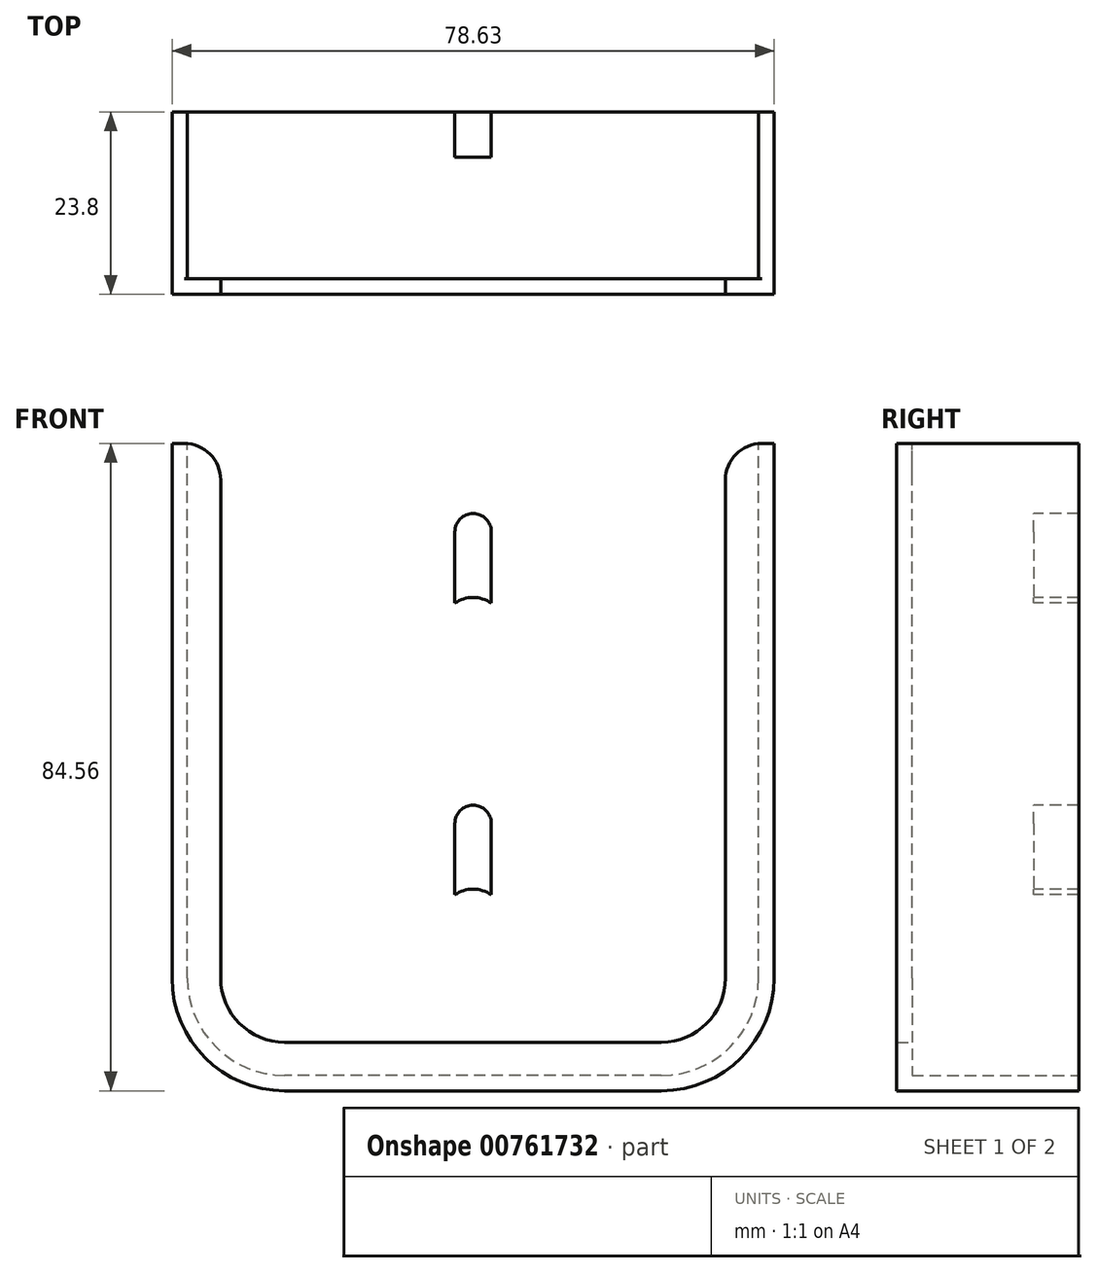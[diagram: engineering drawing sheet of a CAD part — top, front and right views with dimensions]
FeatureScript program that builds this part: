
annotation { "Feature Type Name" : "Feature", "Feature Type Description" : "" }
export const myFeature = defineFeature(function(context is Context, id is Id, definition is map)
    precondition{}
    {
        {
            var Q0;
            Q0=qCreatedBy(makeId("Front.planeOp"),FACE);
            var sketch = newSketch(context, id + "F0", { "sketchPlane" : qUnion([Q0])});
            skLineSegment(sketch, "E0.bottom", {"start": v(-12.7, 0) * mm, "end": v(-61.91, 0) * mm});
            skLineSegment(sketch, "E0.top", {"start": v(-6.35, 88.9) * mm, "end": v(-68.26, 88.9) * mm});
            skLineSegment(sketch, "E0.left", {"start": v(0, 12.7) * mm, "end": v(0, 82.55) * mm});
            skLineSegment(sketch, "E0.right", {"start": v(-74.61, 12.7) * mm, "end": v(-74.61, 82.55) * mm});
            skPoint(sketch, "E1.visualSharp", {"position": v(-74.61, 0) * mm});
            skArc(sketch, "E1.filletArc", {"start": v(-74.61, 12.7) * mm, "mid": v(-70.9, 3.72) * mm, "end": v(-61.91, 0) * mm});
            skPoint(sketch, "E2.visualSharp", {"position": v(0, 0) * mm});
            skArc(sketch, "E2.filletArc", {"start": v(-12.7, 0) * mm, "mid": v(-3.72, 3.72) * mm, "end": v(0, 12.7) * mm});
            skPoint(sketch, "E3.visualSharp", {"position": v(-74.61, 88.9) * mm});
            skArc(sketch, "E3.filletArc", {"start": v(-68.26, 88.9) * mm, "mid": v(-72.75, 87.04) * mm, "end": v(-74.61, 82.55) * mm});
            skPoint(sketch, "E4.visualSharp", {"position": v(0, 88.9) * mm});
            skArc(sketch, "E4.filletArc", {"start": v(0, 82.55) * mm, "mid": v(-1.86, 87.04) * mm, "end": v(-6.35, 88.9) * mm});
            skSolve(sketch);
        }
        {
            var Q0;
            Q0=makeQuery(id+"F0.imprint","IMPRINT",FACE,{"disambiguationData":[TD([[makeQuery(id+"F0.imprint","IMPRINT",EDGE,{"derivedFrom":sQuery(id+"F0.wireOp",EDGE,"E0.bottom")}),-1.0]])]});
            extrude(context, id + "F1", {"entities" : qUnion([Q0]), "depth" : 12.7 * mm, "offsetDistance" : 25.4 * mm});
        }
        {
            var Q0;
            Q0=makeQuery(id+"F1.opExtrude","SWEPT_FACE",FACE,{"disambiguationData":[OSD([sQuery(id+"F0.wireOp",EDGE,"E0.top")])]});
            var Q1;
            Q1=makeQuery(id+"F1.opExtrude","SWEPT_FACE",FACE,{"disambiguationData":[OSD([sQuery(id+"F0.wireOp",EDGE,"E3.filletArc")])]});
            var Q2;
            Q2=makeQuery(id+"F1.opExtrude","SWEPT_FACE",FACE,{"disambiguationData":[OSD([sQuery(id+"F0.wireOp",EDGE,"E4.filletArc")])]});
            var Q3;
            Q3=makeQuery(id+"F1.opExtrude","CAP_FACE",FACE,{"disambiguationData":[OSD([sQuery(id+"F0.wireOp",EDGE,"E0.bottom"),sQuery(id+"F0.wireOp",EDGE,"E0.top"),sQuery(id+"F0.wireOp",EDGE,"E0.left"),sQuery(id+"F0.wireOp",EDGE,"E0.right"),sQuery(id+"F0.wireOp",EDGE,"E1.filletArc"),sQuery(id+"F0.wireOp",EDGE,"E2.filletArc"),sQuery(id+"F0.wireOp",EDGE,"E3.filletArc"),sQuery(id+"F0.wireOp",EDGE,"E4.filletArc")])],"isStart":false});
            shell(context, id + "F2", {"entities" : qUnion([Q0, Q1, Q2, Q3]), "thickness" : 2 * mm, "oppositeDirection" : true});
        }
        {
            var Q0;
            Q0=makeQuery(id+"F1.opExtrude","CAP_FACE",FACE,{"disambiguationData":[OSD([sQuery(id+"F0.wireOp",EDGE,"E0.bottom"),sQuery(id+"F0.wireOp",EDGE,"E0.top"),sQuery(id+"F0.wireOp",EDGE,"E0.left"),sQuery(id+"F0.wireOp",EDGE,"E0.right"),sQuery(id+"F0.wireOp",EDGE,"E1.filletArc"),sQuery(id+"F0.wireOp",EDGE,"E2.filletArc"),sQuery(id+"F0.wireOp",EDGE,"E3.filletArc"),sQuery(id+"F0.wireOp",EDGE,"E4.filletArc")])],"isStart":false});
            var sketch = newSketch(context, id + "F3", { "sketchPlane" : qUnion([Q0])});
            skLineSegment(sketch, "E5.0", {"start": v(-76.62, 12.7) * mm, "end": v(-76.62, 82.55) * mm});
            skArc(sketch, "E6.0", {"start": v(-76.62, 12.7) * mm, "mid": v(-72.31, 2.3) * mm, "end": v(-61.91, -2) * mm});
            skLineSegment(sketch, "E7.0", {"start": v(-12.7, -2) * mm, "end": v(-61.91, -2) * mm});
            skArc(sketch, "E8.0", {"start": v(-12.7, -2) * mm, "mid": v(-2.3, 2.3) * mm, "end": v(2, 12.7) * mm});
            skLineSegment(sketch, "E9.0", {"start": v(2, 12.7) * mm, "end": v(2, 82.55) * mm});
            skLineSegment(sketch, "E10.0", {"start": v(-70.27, 12.7) * mm, "end": v(-70.27, 77.79) * mm});
            skLineSegment(sketch, "E10.1", {"start": v(-4.34, 12.7) * mm, "end": v(-4.34, 77.79) * mm});
            skArc(sketch, "E10.2", {"start": v(-12.7, 4.34) * mm, "mid": v(-6.8, 6.8) * mm, "end": v(-4.34, 12.7) * mm});
            skLineSegment(sketch, "E10.3", {"start": v(-12.7, 4.34) * mm, "end": v(-61.91, 4.34) * mm});
            skArc(sketch, "E10.4", {"start": v(-70.27, 12.7) * mm, "mid": v(-67.82, 6.8) * mm, "end": v(-61.91, 4.34) * mm});
            skLineSegment(sketch, "E11", {"start": v(-76.62, 82.55) * mm, "end": v(-75.03, 82.55) * mm});
            skLineSegment(sketch, "E12", {"start": v(2, 82.55) * mm, "end": v(0.42, 82.55) * mm});
            skPoint(sketch, "E13.visualSharp", {"position": v(-70.27, 82.55) * mm});
            skArc(sketch, "E13.filletArc", {"start": v(-70.27, 77.79) * mm, "mid": v(-71.66, 81.16) * mm, "end": v(-75.03, 82.55) * mm});
            skPoint(sketch, "E14.visualSharp", {"position": v(-4.34, 82.55) * mm});
            skArc(sketch, "E14.filletArc", {"start": v(0.42, 82.55) * mm, "mid": v(-2.95, 81.16) * mm, "end": v(-4.34, 77.79) * mm});
            skSolve(sketch);
        }
        {
            var Q0;
            {var subQ6=sQuery(id+"F3.wireOp",EDGE,"E10.0");Q0=makeQuery(id+"F3.imprint","IMPRINT",FACE,{"disambiguationData":[TD([[makeQuery(id+"F3.imprint","IMPRINT",EDGE,{"derivedFrom":subQ6}),1.0]])]});}
            var Q1;
            Q1=makeQuery(id+"F3.imprint","IMPRINT",FACE,{"disambiguationData":[TD([[makeQuery(id+"F3.imprint","IMPRINT",EDGE,{"derivedFrom":sQuery(id+"F3.wireOp",EDGE,"E5.0")}),-1.0]])]});
            extrude(context, id + "F4", {"entities" : qUnion([Q0, Q1]), "operationType" : NewBodyOperationType.ADD, "depth" : 2 * mm, "offsetDistance" : 25.4 * mm});
        }
        {
            var Q0;
            Q0=makeQuery(id+"F1.opExtrude","CAP_FACE",FACE,{"disambiguationData":[OSD([sQuery(id+"F0.wireOp",EDGE,"E0.bottom"),sQuery(id+"F0.wireOp",EDGE,"E0.top"),sQuery(id+"F0.wireOp",EDGE,"E0.left"),sQuery(id+"F0.wireOp",EDGE,"E0.right"),sQuery(id+"F0.wireOp",EDGE,"E1.filletArc"),sQuery(id+"F0.wireOp",EDGE,"E2.filletArc"),sQuery(id+"F0.wireOp",EDGE,"E3.filletArc"),sQuery(id+"F0.wireOp",EDGE,"E4.filletArc")])],"isStart":true});
            extrude(context, id + "F5", {"entities" : qUnion([Q0]), "operationType" : NewBodyOperationType.ADD, "depth" : 7.1 * mm, "offsetDistance" : 25.4 * mm});
        }
        {
            var Q0;
            Q0=makeQuery(id+"F2.opShell","OFFSET_FACE",FACE,{"disambiguationData":[OSD([sQuery(id+"F0.wireOp",EDGE,"E0.bottom"),sQuery(id+"F0.wireOp",EDGE,"E0.top"),sQuery(id+"F0.wireOp",EDGE,"E0.left"),sQuery(id+"F0.wireOp",EDGE,"E0.right"),sQuery(id+"F0.wireOp",EDGE,"E1.filletArc"),sQuery(id+"F0.wireOp",EDGE,"E2.filletArc"),sQuery(id+"F0.wireOp",EDGE,"E3.filletArc"),sQuery(id+"F0.wireOp",EDGE,"E4.filletArc")])]});
            var sketch = newSketch(context, id + "F6", { "sketchPlane" : qUnion([Q0])});
            skCircle(sketch, "E15", {"center": v(-37.3, 20.22) * mm, "radius": 4.13 * mm});
            skPoint(sketch, "E15.centerSnap0", {"position": v(-37.3, 88.9) * mm});
            skLineSegment(sketch, "E16", {"start": v(-37.3, 20.22) * mm, "end": v(-37.3, 32.92) * mm});
            skArc(sketch, "E17.0.startCap", {"start": v(-34.93, 20.22) * mm, "mid": v(-37.3, 17.84) * mm, "end": v(-39.69, 20.22) * mm});
            skArc(sketch, "E17.0.endCap", {"start": v(-39.69, 32.92) * mm, "mid": v(-37.3, 35.3) * mm, "end": v(-34.93, 32.92) * mm});
            skLineSegment(sketch, "E17.0.left", {"start": v(-39.69, 20.22) * mm, "end": v(-39.69, 32.92) * mm});
            skLineSegment(sketch, "E17.0.right", {"start": v(-34.93, 20.22) * mm, "end": v(-34.93, 32.92) * mm});
            skCircle(sketch, "E18", {"center": v(-37.3, 58.32) * mm, "radius": 4.13 * mm});
            skLineSegment(sketch, "E19", {"start": v(-37.3, 58.32) * mm, "end": v(-37.3, 71.02) * mm});
            skArc(sketch, "E20.0.startCap", {"start": v(-34.93, 58.32) * mm, "mid": v(-37.3, 55.94) * mm, "end": v(-39.69, 58.32) * mm});
            skArc(sketch, "E20.0.endCap", {"start": v(-39.69, 71.02) * mm, "mid": v(-37.3, 73.4) * mm, "end": v(-34.93, 71.02) * mm});
            skLineSegment(sketch, "E20.0.left", {"start": v(-39.69, 58.32) * mm, "end": v(-39.69, 71.02) * mm});
            skLineSegment(sketch, "E20.0.right", {"start": v(-34.93, 58.32) * mm, "end": v(-34.93, 71.02) * mm});
            skArc(sketch, "E21.0.startCap", {"start": v(-33.18, 20.22) * mm, "mid": v(-37.3, 16.1) * mm, "end": v(-41.43, 20.22) * mm});
            skArc(sketch, "E22.0.startCap", {"start": v(-33.18, 58.32) * mm, "mid": v(-37.3, 54.2) * mm, "end": v(-41.43, 58.32) * mm});
            skSolve(sketch);
        }
        {
            var Q0;
            {var subQ5=sQuery(id+"F6.wireOp",EDGE,"E17.0.startCap");Q0=makeQuery(id+"F6.imprint","IMPRINT",FACE,{"disambiguationData":[TD([[makeQuery(id+"F6.imprint","IMPRINT",EDGE,{"derivedFrom":subQ5}),1.0]])]});}
            var Q1;
            {var subQ1=sQuery(id+"F6.wireOp",EDGE,"E17.0.endCap");Q1=makeQuery(id+"F6.imprint","IMPRINT",FACE,{"disambiguationData":[TD([[makeQuery(id+"F6.imprint","IMPRINT",EDGE,{"derivedFrom":subQ1}),-1.0]])]});}
            var Q2;
            {var subQ5=sQuery(id+"F6.wireOp",EDGE,"E20.0.startCap");Q2=makeQuery(id+"F6.imprint","IMPRINT",FACE,{"disambiguationData":[TD([[makeQuery(id+"F6.imprint","IMPRINT",EDGE,{"derivedFrom":subQ5}),1.0]])]});}
            var Q3;
            {var subQ1=sQuery(id+"F6.wireOp",EDGE,"E20.0.endCap");Q3=makeQuery(id+"F6.imprint","IMPRINT",FACE,{"disambiguationData":[TD([[makeQuery(id+"F6.imprint","IMPRINT",EDGE,{"derivedFrom":subQ1}),-1.0]])]});}
            var Q4;
            {var subQ0=sQuery(id+"F6.wireOp",EDGE,"E20.0.startCap");Q4=makeQuery(id+"F6.imprint","IMPRINT",FACE,{"disambiguationData":[TD([[makeQuery(id+"F6.imprint","IMPRINT",EDGE,{"derivedFrom":subQ0}),-1.0]])]});}
            var Q5;
            {var subQ0=sQuery(id+"F6.wireOp",EDGE,"E17.0.startCap");Q5=makeQuery(id+"F6.imprint","IMPRINT",FACE,{"disambiguationData":[TD([[makeQuery(id+"F6.imprint","IMPRINT",EDGE,{"derivedFrom":subQ0}),-1.0]])]});}
            extrude(context, id + "F7", {"entities" : qUnion([Q0, Q1, Q2, Q3, Q4, Q5]), "operationType" : NewBodyOperationType.REMOVE, "endBound" : BoundingType.THROUGH_ALL, "oppositeDirection" : true, "depth" : 25.4 * mm, "offsetDistance" : 25.4 * mm});
        }
        {
            var Q0;
            Q0=makeQuery(id+"F2.opShell","OFFSET_FACE",FACE,{"disambiguationData":[OSD([sQuery(id+"F0.wireOp",EDGE,"E0.bottom"),sQuery(id+"F0.wireOp",EDGE,"E0.top"),sQuery(id+"F0.wireOp",EDGE,"E0.left"),sQuery(id+"F0.wireOp",EDGE,"E0.right"),sQuery(id+"F0.wireOp",EDGE,"E1.filletArc"),sQuery(id+"F0.wireOp",EDGE,"E2.filletArc"),sQuery(id+"F0.wireOp",EDGE,"E3.filletArc"),sQuery(id+"F0.wireOp",EDGE,"E4.filletArc")])]});
            var sketch = newSketch(context, id + "F8", { "sketchPlane" : qUnion([Q0])});
            skLineSegment(sketch, "E23", {"start": v(-37.3, 58.32) * mm, "end": v(-37.3, 71.02) * mm});
            skLineSegment(sketch, "E24", {"start": v(-37.3, 20.22) * mm, "end": v(-37.3, 32.92) * mm});
            skArc(sketch, "E25.0.startCap", {"start": v(-33.18, 20.22) * mm, "mid": v(-37.3, 16.1) * mm, "end": v(-41.43, 20.22) * mm});
            skArc(sketch, "E25.0.endCap", {"start": v(-41.43, 32.92) * mm, "mid": v(-37.3, 37.05) * mm, "end": v(-33.18, 32.92) * mm});
            skLineSegment(sketch, "E25.0.left", {"start": v(-41.43, 20.22) * mm, "end": v(-41.43, 32.92) * mm});
            skLineSegment(sketch, "E25.0.right", {"start": v(-33.18, 20.22) * mm, "end": v(-33.18, 32.92) * mm});
            skArc(sketch, "E25.1.startCap", {"start": v(-33.18, 58.32) * mm, "mid": v(-37.3, 54.2) * mm, "end": v(-41.43, 58.32) * mm});
            skArc(sketch, "E25.1.endCap", {"start": v(-41.43, 71.02) * mm, "mid": v(-37.3, 75.15) * mm, "end": v(-33.18, 71.02) * mm});
            skLineSegment(sketch, "E25.1.left", {"start": v(-41.43, 58.32) * mm, "end": v(-41.43, 71.02) * mm});
            skLineSegment(sketch, "E25.1.right", {"start": v(-33.18, 58.32) * mm, "end": v(-33.18, 71.02) * mm});
            skSolve(sketch);
        }
        {
            var Q0;
            Q0 = qSketchRegion(id + "F8", true);
            extrude(context, id + "F9", {"entities" : qUnion([Q0]), "operationType" : NewBodyOperationType.REMOVE, "oppositeDirection" : true, "depth" : 3.17 * mm, "offsetDistance" : 25.4 * mm});
        }
    });
